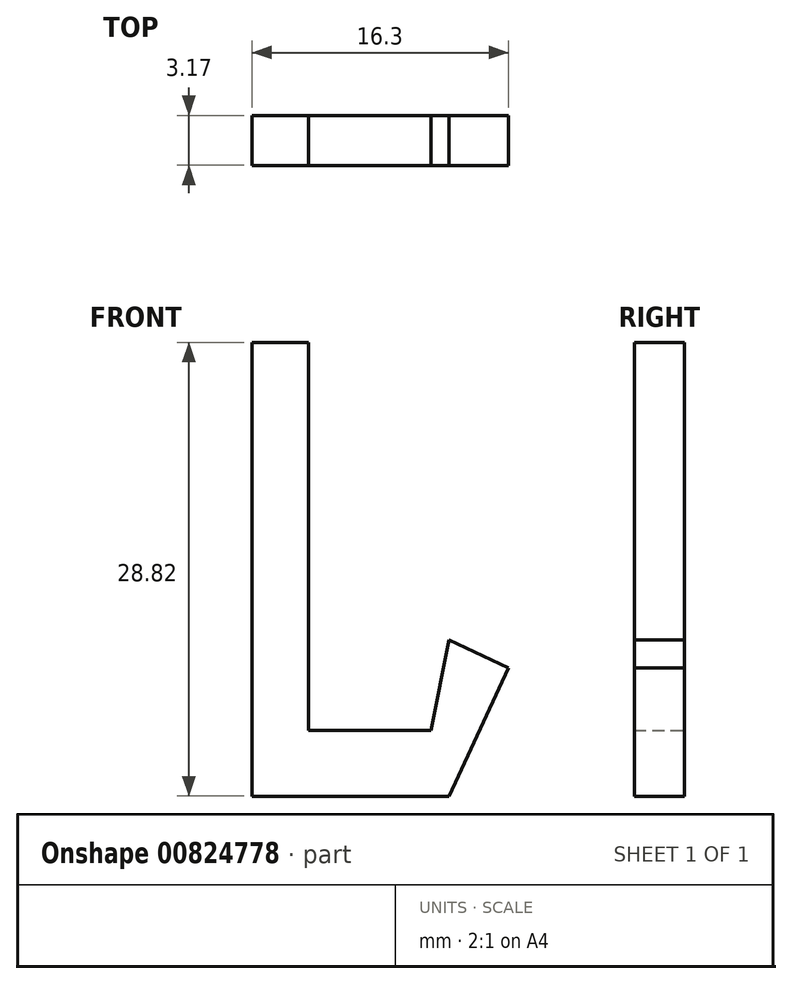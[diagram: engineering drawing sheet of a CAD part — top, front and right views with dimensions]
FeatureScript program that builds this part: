
annotation { "Feature Type Name" : "Feature", "Feature Type Description" : "" }
export const myFeature = defineFeature(function(context is Context, id is Id, definition is map)
    precondition{}
    {
        {
            var Q0;
            Q0=qCreatedBy(makeId("Front.planeOp"),FACE);
            var sketch = newSketch(context, id + "F0", { "sketchPlane" : qUnion([Q0])});
            skLineSegment(sketch, "E0", {"start": v(37.64, 7.3) * mm, "end": v(29.86, 7.3) * mm});
            skLineSegment(sketch, "E1", {"start": v(29.86, 7.3) * mm, "end": v(29.86, 31.95) * mm});
            skLineSegment(sketch, "E2", {"start": v(29.86, 31.95) * mm, "end": v(26.26, 31.95) * mm});
            skLineSegment(sketch, "E3", {"start": v(26.26, 31.95) * mm, "end": v(26.26, 3.13) * mm});
            skLineSegment(sketch, "E4", {"start": v(26.26, 3.13) * mm, "end": v(38.77, 3.13) * mm});
            skLineSegment(sketch, "E5", {"start": v(38.77, 3.13) * mm, "end": v(42.56, 11.28) * mm});
            skLineSegment(sketch, "E6", {"start": v(42.56, 11.28) * mm, "end": v(38.77, 13.04) * mm});
            skLineSegment(sketch, "E7", {"start": v(38.77, 13.04) * mm, "end": v(37.64, 7.3) * mm});
            skSolve(sketch);
        }
        {
            var Q0;
            Q0 = qSketchRegion(id + "F0", true);
            extrude(context, id + "F1", {"entities" : qUnion([Q0]), "depth" : 3.17 * mm, "offsetDistance" : 25.4 * mm});
        }
    });
